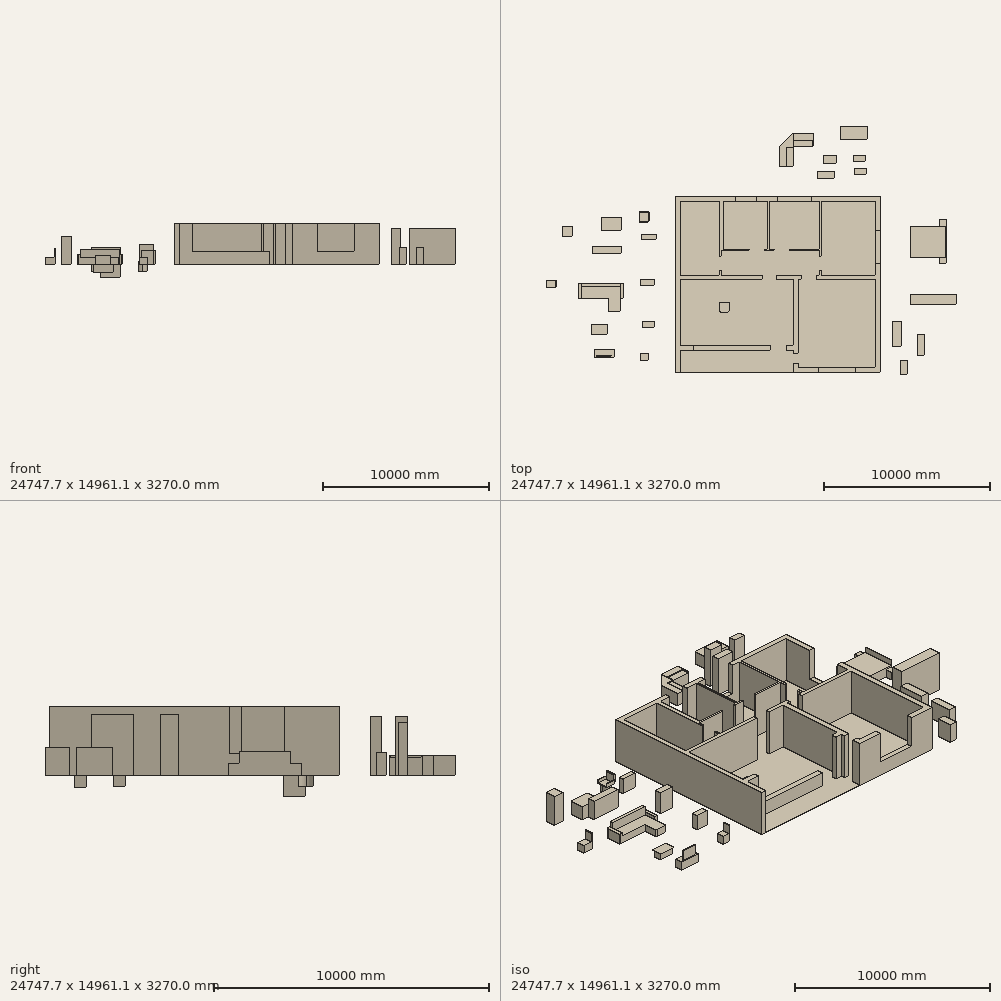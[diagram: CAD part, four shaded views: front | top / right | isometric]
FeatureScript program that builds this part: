
annotation { "Feature Type Name" : "Feature", "Feature Type Description" : "" }
export const myFeature = defineFeature(function(context is Context, id is Id, definition is map)
    precondition{}
    {
        {
            var Q0;
            Q0=qCreatedBy(makeId("Top.planeOp"),FACE);
            var sketch = newSketch(context, id + "F0", { "sketchPlane" : qUnion([Q0])});
            skLineSegment(sketch, "E0", {"start": v(0, 0) * mm, "end": v(12365, 0) * mm});
            skLineSegment(sketch, "E1", {"start": v(12365, 0) * mm, "end": v(12365, 10595) * mm});
            skLineSegment(sketch, "E2", {"start": v(12365, 10595) * mm, "end": v(0, 10595) * mm});
            skLineSegment(sketch, "E3", {"start": v(0, 10595) * mm, "end": v(0, 0) * mm});
            skLineSegment(sketch, "E4", {"start": v(12062.5, 10292.5) * mm, "end": v(12062.5, 5802.5) * mm});
            skLineSegment(sketch, "E5", {"start": v(12062.5, 302.5) * mm, "end": v(7427.5, 302.5) * mm});
            skLineSegment(sketch, "E6", {"start": v(7427.5, 302.5) * mm, "end": v(7427.5, 5562.5) * mm});
            skLineSegment(sketch, "E7", {"start": v(12062.5, 10292.5) * mm, "end": v(8802.5, 10292.5) * mm});
            skLineSegment(sketch, "E8", {"start": v(302.5, 10292.5) * mm, "end": v(302.5, 5802.5) * mm});
            skLineSegment(sketch, "E9", {"start": v(12062.5, 5562.5) * mm, "end": v(7427.5, 5562.5) * mm});
            skLineSegment(sketch, "E10", {"start": v(12062.5, 5802.5) * mm, "end": v(8802.5, 5802.5) * mm});
            skPoint(sketch, "E10.endSnap0", {"position": v(302.5, 5146.25) * mm});
            skLineSegment(sketch, "E11", {"start": v(7125, 5562.5) * mm, "end": v(7125, 1617.5) * mm});
            skLineSegment(sketch, "E12", {"start": v(8802.5, 10292.5) * mm, "end": v(8802.5, 5802.5) * mm});
            skLineSegment(sketch, "E13", {"start": v(8687.5, 10292.5) * mm, "end": v(8687.5, 7427.5) * mm});
            skLineSegment(sketch, "E14", {"start": v(8687.5, 7312.5) * mm, "end": v(2802.5, 7312.5) * mm});
            skLineSegment(sketch, "E15", {"start": v(2687.5, 10292.5) * mm, "end": v(2687.5, 7312.5) * mm});
            skLineSegment(sketch, "E16", {"start": v(2927.5, 10292.5) * mm, "end": v(2927.5, 7427.5) * mm});
            skLineSegment(sketch, "E17", {"start": v(2927.5, 7427.5) * mm, "end": v(5562.5, 7427.5) * mm});
            skLineSegment(sketch, "E18", {"start": v(2687.5, 7312.5) * mm, "end": v(2687.5, 5802.5) * mm});
            skLineSegment(sketch, "E19", {"start": v(2802.5, 7312.5) * mm, "end": v(2802.5, 5802.5) * mm});
            skLineSegment(sketch, "E20", {"start": v(5677.5, 10292.5) * mm, "end": v(5677.5, 7427.5) * mm});
            skLineSegment(sketch, "E21", {"start": v(5562.5, 10292.5) * mm, "end": v(5562.5, 7427.5) * mm});
            skLineSegment(sketch, "E22.trimOffspring", {"start": v(2687.5, 10292.5) * mm, "end": v(302.5, 10292.5) * mm});
            skLineSegment(sketch, "E23.trimOffspring", {"start": v(5562.5, 10292.5) * mm, "end": v(2927.5, 10292.5) * mm});
            skLineSegment(sketch, "E24.trimOffspring", {"start": v(5677.5, 7427.5) * mm, "end": v(8687.5, 7427.5) * mm});
            skLineSegment(sketch, "E25.trimOffspring", {"start": v(8687.5, 10292.5) * mm, "end": v(5677.5, 10292.5) * mm});
            skLineSegment(sketch, "E26.trimOffspring", {"start": v(8687.5, 7312.5) * mm, "end": v(8687.5, 5802.5) * mm});
            skLineSegment(sketch, "E27.trimOffspring", {"start": v(12062.5, 5562.5) * mm, "end": v(12062.5, 302.5) * mm});
            skLineSegment(sketch, "E28.trimOffspring", {"start": v(302.5, 5562.5) * mm, "end": v(302.5, 1617.5) * mm});
            skLineSegment(sketch, "E29.trimOffspring", {"start": v(2687.5, 5802.5) * mm, "end": v(302.5, 5802.5) * mm});
            skLineSegment(sketch, "E30", {"start": v(302.5, 1315) * mm, "end": v(7125, 1315) * mm});
            skLineSegment(sketch, "E31", {"start": v(302.5, 1617.5) * mm, "end": v(7125, 1617.5) * mm});
            skLineSegment(sketch, "E32.trimOffspring", {"start": v(302.5, 1315) * mm, "end": v(302.5, 0) * mm});
            skLineSegment(sketch, "E33.trimOffspring", {"start": v(7125, 1315) * mm, "end": v(7125, 0) * mm});
            skLineSegment(sketch, "E34.trimOffspring", {"start": v(7125, 5562.5) * mm, "end": v(302.5, 5562.5) * mm});
            skLineSegment(sketch, "E35", {"start": v(8687.5, 7000) * mm, "end": v(8802.5, 7000) * mm});
            skLineSegment(sketch, "E36", {"start": v(8687.5, 6115) * mm, "end": v(8802.5, 6115) * mm});
            skLineSegment(sketch, "E37.trimOffspring", {"start": v(8687.5, 5802.5) * mm, "end": v(2802.5, 5802.5) * mm});
            skLineSegment(sketch, "E38", {"start": v(7615, 5802.5) * mm, "end": v(7615, 5562.5) * mm});
            skLineSegment(sketch, "E39", {"start": v(8500, 5802.5) * mm, "end": v(8500, 5562.5) * mm});
            skLineSegment(sketch, "E40", {"start": v(5990, 7427.5) * mm, "end": v(5990, 7312.5) * mm});
            skLineSegment(sketch, "E41", {"start": v(6875, 7427.5) * mm, "end": v(6875, 7312.5) * mm});
            skLineSegment(sketch, "E42", {"start": v(5375, 7427.5) * mm, "end": v(5375, 7312.5) * mm});
            skLineSegment(sketch, "E43", {"start": v(4490, 7427.5) * mm, "end": v(4490, 7312.5) * mm});
            skLineSegment(sketch, "E44", {"start": v(6125, 5802.5) * mm, "end": v(6125, 5562.5) * mm});
            skLineSegment(sketch, "E45", {"start": v(5240, 5802.5) * mm, "end": v(5240, 5562.5) * mm});
            skLineSegment(sketch, "E46", {"start": v(8615, 302.5) * mm, "end": v(8615, 0) * mm});
            skLineSegment(sketch, "E47", {"start": v(10875, 302.5) * mm, "end": v(10875, 0) * mm});
            skLineSegment(sketch, "E48", {"start": v(1102.5, 1617.5) * mm, "end": v(1102.5, 1315) * mm});
            skLineSegment(sketch, "E49", {"start": v(6725, 1617.5) * mm, "end": v(6725, 1315) * mm});
            skLineSegment(sketch, "E50", {"start": v(7125, 1108.75) * mm, "end": v(7427.5, 1108.75) * mm});
            skLineSegment(sketch, "E51", {"start": v(7125, 508.75) * mm, "end": v(7427.5, 508.75) * mm});
            skLineSegment(sketch, "E52", {"start": v(12062.5, 8572.5) * mm, "end": v(12365, 8572.5) * mm});
            skLineSegment(sketch, "E53", {"start": v(12062.5, 6562.5) * mm, "end": v(12365, 6562.5) * mm});
            skArc(sketch, "E54", {"start": v(8802.5, 7000) * mm, "mid": v(9428.29, 6740.79) * mm, "end": v(9687.5, 6115) * mm});
            skArc(sketch, "E55", {"start": v(6875, 7427.5) * mm, "mid": v(6615.79, 8053.29) * mm, "end": v(5990, 8312.5) * mm});
            skArc(sketch, "E56", {"start": v(4490, 7427.5) * mm, "mid": v(4749.21, 8053.29) * mm, "end": v(5375, 8312.5) * mm});
            skArc(sketch, "E57", {"start": v(5240, 5562.5) * mm, "mid": v(5499.21, 4936.71) * mm, "end": v(6125, 4677.5) * mm});
            skArc(sketch, "E58", {"start": v(7427.5, 1108.75) * mm, "mid": v(7851.76, 933.01) * mm, "end": v(8027.5, 508.75) * mm});
            skLineSegment(sketch, "E59", {"start": v(5715, 1617.5) * mm, "end": v(5715, 1315) * mm});
            skArc(sketch, "E60", {"start": v(5715, 1617.5) * mm, "mid": v(6010.82, 2331.68) * mm, "end": v(6725, 2627.5) * mm});
            skLineSegment(sketch, "E61", {"start": v(2687.5, 7000) * mm, "end": v(2802.5, 7000) * mm});
            skLineSegment(sketch, "E62", {"start": v(2687.5, 6115) * mm, "end": v(2802.5, 6115) * mm});
            skArc(sketch, "E63", {"start": v(8500, 5562.5) * mm, "mid": v(8240.79, 4936.71) * mm, "end": v(7615, 4677.5) * mm});
            skLineSegment(sketch, "E64", {"start": v(6177.5, 10595) * mm, "end": v(6177.5, 10292.5) * mm});
            skLineSegment(sketch, "E65", {"start": v(8187.5, 10595) * mm, "end": v(8187.5, 10292.5) * mm});
            skLineSegment(sketch, "E66", {"start": v(3615, 10595) * mm, "end": v(3615, 10292.5) * mm});
            skLineSegment(sketch, "E67", {"start": v(4875, 10595) * mm, "end": v(4875, 10292.5) * mm});
            skSolve(sketch);
        }
        {
            var Q0;
            Q0=qCreatedBy(makeId("Top.planeOp"),FACE);
            var sketch = newSketch(context, id + "F1", { "sketchPlane" : qUnion([Q0])});
            skLineSegment(sketch, "E68.bottom", {"start": v(0, 0) * mm, "end": v(12364.74, 0) * mm});
            skLineSegment(sketch, "E68.top", {"start": v(0, 10595.95) * mm, "end": v(12364.74, 10595.95) * mm});
            skLineSegment(sketch, "E68.left", {"start": v(0, 0) * mm, "end": v(0, 10595.95) * mm});
            skLineSegment(sketch, "E68.right", {"start": v(12364.74, 0) * mm, "end": v(12364.74, 10595.95) * mm});
            skSolve(sketch);
        }
        {
            var Q0;
            {var subQ12=sQuery(id+"F0.wireOp",EDGE,"E10");Q0=makeQuery(id+"F0.imprint","IMPRINT",FACE,{"disambiguationData":[TD([[makeQuery(id+"F0.imprint","IMPRINT",EDGE,{"derivedFrom":subQ12}),1.0]])]});}
            var Q1;
            {var subQ8=sQuery(id+"F0.wireOp",EDGE,"E11");Q1=makeQuery(id+"F0.imprint","IMPRINT",FACE,{"disambiguationData":[TD([[makeQuery(id+"F0.imprint","IMPRINT",EDGE,{"derivedFrom":subQ8}),1.0]])]});}
            var Q2;
            {var subQ7=sQuery(id+"F0.wireOp",EDGE,"E46");Q2=makeQuery(id+"F0.imprint","IMPRINT",FACE,{"disambiguationData":[TD([[makeQuery(id+"F0.imprint","IMPRINT",EDGE,{"derivedFrom":subQ7}),-1.0]])]});}
            var Q3;
            {var subQ21=sQuery(id+"F0.wireOp",EDGE,"E3");Q3=makeQuery(id+"F0.imprint","IMPRINT",FACE,{"disambiguationData":[TD([[makeQuery(id+"F0.imprint","IMPRINT",EDGE,{"derivedFrom":subQ21}),1.0]])]});}
            var Q4;
            {var subQ3=sQuery(id+"F0.wireOp",EDGE,"E20");Q4=makeQuery(id+"F0.imprint","IMPRINT",FACE,{"disambiguationData":[TD([[makeQuery(id+"F0.imprint","IMPRINT",EDGE,{"derivedFrom":subQ3}),-1.0]])]});}
            var Q5;
            {var subQ4=sQuery(id+"F0.wireOp",EDGE,"E7");Q5=makeQuery(id+"F0.imprint","IMPRINT",FACE,{"disambiguationData":[TD([[makeQuery(id+"F0.imprint","IMPRINT",EDGE,{"derivedFrom":subQ4}),-1.0]])]});}
            extrude(context, id + "F2", {"entities" : qUnion([Q0, Q1, Q2, Q3, Q4, Q5]), "depth" : 2500 * mm});
        }
        {
            var Q0;
            {var subQ0=sQuery(id+"F0.wireOp",EDGE,"E52");Q0=makeQuery(id+"F0.imprint","IMPRINT",FACE,{"disambiguationData":[TD([[makeQuery(id+"F0.imprint","IMPRINT",EDGE,{"derivedFrom":subQ0}),-1.0]])]});}
            var Q1;
            {var subQ0=sQuery(id+"F0.wireOp",EDGE,"E46");Q1=makeQuery(id+"F0.imprint","IMPRINT",FACE,{"disambiguationData":[TD([[makeQuery(id+"F0.imprint","IMPRINT",EDGE,{"derivedFrom":subQ0}),1.0]])]});}
            var Q2;
            {var subQ0=sQuery(id+"F0.wireOp",EDGE,"E48");Q2=makeQuery(id+"F0.imprint","IMPRINT",FACE,{"disambiguationData":[TD([[makeQuery(id+"F0.imprint","IMPRINT",EDGE,{"derivedFrom":subQ0}),1.0]])]});}
            var Q3;
            {var subQ0=sQuery(id+"F0.wireOp",EDGE,"E66");Q3=makeQuery(id+"F0.imprint","IMPRINT",FACE,{"disambiguationData":[TD([[makeQuery(id+"F0.imprint","IMPRINT",EDGE,{"derivedFrom":subQ0}),1.0]])]});}
            var Q4;
            {var subQ0=sQuery(id+"F0.wireOp",EDGE,"E64");Q4=makeQuery(id+"F0.imprint","IMPRINT",FACE,{"disambiguationData":[TD([[makeQuery(id+"F0.imprint","IMPRINT",EDGE,{"derivedFrom":subQ0}),1.0]])]});}
            extrude(context, id + "F3", {"entities" : qUnion([Q0, Q1, Q2, Q3, Q4]), "operationType" : NewBodyOperationType.ADD, "depth" : 800 * mm});
        }
        {
            var Q0;
            Q0 = qSketchRegion(id + "F1", true);
            extrude(context, id + "F4", {"entities" : qUnion([Q0]), "operationType" : NewBodyOperationType.ADD, "depth" : 25 * mm});
        }
        {
            var Q0;
            {var subQ3=sQuery(id+"F0.wireOp",EDGE,"E7");var subQ55=sQuery(id+"F1.wireOp",EDGE,"E68.bottom");Q0=makeQuery(id+"F4.boolean.opBoolean","SPLIT",FACE,{"disambiguationData":[TD([makeQuery(id+"F2.opExtrude","SWEPT_FACE",FACE,{"disambiguationData":[OSD([subQ3])]})])],"derivedFrom":makeQuery(id+"F4.opExtrude","CAP_FACE",FACE,{"disambiguationData":[OSD([subQ55,sQuery(id+"F1.wireOp",EDGE,"E68.top"),sQuery(id+"F1.wireOp",EDGE,"E68.left"),sQuery(id+"F1.wireOp",EDGE,"E68.right")])],"isStart":false})});}
            var sketch = newSketch(context, id + "F5", { "sketchPlane" : qUnion([Q0])});
            skLineSegment(sketch, "E69.bottom", {"start": v(2725.04, 4227.94) * mm, "end": v(3195.04, 4227.94) * mm});
            skLineSegment(sketch, "E69.top", {"start": v(2725.04, 3627.94) * mm, "end": v(3195.04, 3627.94) * mm});
            skLineSegment(sketch, "E69.left", {"start": v(2675.04, 4177.94) * mm, "end": v(2675.04, 3677.94) * mm});
            skLineSegment(sketch, "E69.right", {"start": v(3245.04, 4177.94) * mm, "end": v(3245.04, 3677.94) * mm});
            skPoint(sketch, "E70.visualSharp", {"position": v(2675.04, 4227.94) * mm});
            skArc(sketch, "E70.filletArc", {"start": v(2725.04, 4227.94) * mm, "mid": v(2689.69, 4213.3) * mm, "end": v(2675.04, 4177.94) * mm});
            skPoint(sketch, "E71.visualSharp", {"position": v(3245.04, 4227.94) * mm});
            skArc(sketch, "E71.filletArc", {"start": v(3245.04, 4177.94) * mm, "mid": v(3230.4, 4213.3) * mm, "end": v(3195.04, 4227.94) * mm});
            skPoint(sketch, "E72.visualSharp", {"position": v(3245.04, 3627.94) * mm});
            skArc(sketch, "E72.filletArc", {"start": v(3195.04, 3627.94) * mm, "mid": v(3230.4, 3642.58) * mm, "end": v(3245.04, 3677.94) * mm});
            skPoint(sketch, "E73.visualSharp", {"position": v(2675.04, 3627.94) * mm});
            skArc(sketch, "E73.filletArc", {"start": v(2675.04, 3677.94) * mm, "mid": v(2689.69, 3642.58) * mm, "end": v(2725.04, 3627.94) * mm});
            skSolve(sketch);
        }
        {
            var Q0;
            Q0 = qSketchRegion(id + "F5", true);
            extrude(context, id + "F6", {"entities" : qUnion([Q0]), "depth" : 400 * mm});
        }
        {
            var Q0;
            {var subQ3=sQuery(id+"F0.wireOp",EDGE,"E7");var subQ55=sQuery(id+"F1.wireOp",EDGE,"E68.bottom");Q0=makeQuery(id+"F4.boolean.opBoolean","SPLIT",FACE,{"disambiguationData":[TD([makeQuery(id+"F2.opExtrude","SWEPT_FACE",FACE,{"disambiguationData":[OSD([subQ3])]})])],"derivedFrom":makeQuery(id+"F4.opExtrude","CAP_FACE",FACE,{"disambiguationData":[OSD([subQ55,sQuery(id+"F1.wireOp",EDGE,"E68.top"),sQuery(id+"F1.wireOp",EDGE,"E68.left"),sQuery(id+"F1.wireOp",EDGE,"E68.right")])],"isStart":false})});}
            var sketch = newSketch(context, id + "F7", { "sketchPlane" : qUnion([Q0])});
            skLineSegment(sketch, "E74", {"start": v(-5864.13, 4489.84) * mm, "end": v(-5864.13, 5289.84) * mm});
            skLineSegment(sketch, "E75", {"start": v(-5814.13, 5339.84) * mm, "end": v(-3164.13, 5339.84) * mm});
            skLineSegment(sketch, "E76", {"start": v(-3114.13, 5289.84) * mm, "end": v(-3114.13, 4489.84) * mm});
            skLineSegment(sketch, "E77", {"start": v(-3164.13, 4439.84) * mm, "end": v(-3314.13, 4439.84) * mm});
            skLineSegment(sketch, "E78", {"start": v(-3314.13, 4439.84) * mm, "end": v(-3314.13, 3689.84) * mm});
            skLineSegment(sketch, "E79", {"start": v(-3364.13, 3639.84) * mm, "end": v(-3964.13, 3639.84) * mm});
            skLineSegment(sketch, "E80", {"start": v(-4014.13, 3689.84) * mm, "end": v(-4014.13, 4439.84) * mm});
            skLineSegment(sketch, "E81", {"start": v(-4014.13, 4439.84) * mm, "end": v(-5814.13, 4439.84) * mm});
            skLineSegment(sketch, "E82", {"start": v(-4014.13, 4439.84) * mm, "end": v(-3314.13, 4439.84) * mm, "construction": true});
            skLineSegment(sketch, "E83", {"start": v(-5664.13, 5339.84) * mm, "end": v(-5664.13, 4439.84) * mm});
            skLineSegment(sketch, "E84", {"start": v(-3314.13, 4439.84) * mm, "end": v(-3314.13, 5339.84) * mm});
            skLineSegment(sketch, "E85", {"start": v(-5664.13, 5139.84) * mm, "end": v(-3314.13, 5139.84) * mm});
            skPoint(sketch, "E86.visualSharp", {"position": v(-5864.13, 4439.84) * mm});
            skArc(sketch, "E86.filletArc", {"start": v(-5864.13, 4489.84) * mm, "mid": v(-5849.48, 4454.48) * mm, "end": v(-5814.13, 4439.84) * mm});
            skPoint(sketch, "E87.visualSharp", {"position": v(-4014.13, 3639.84) * mm});
            skArc(sketch, "E87.filletArc", {"start": v(-4014.13, 3689.84) * mm, "mid": v(-3999.48, 3654.48) * mm, "end": v(-3964.13, 3639.84) * mm});
            skPoint(sketch, "E88.visualSharp", {"position": v(-3314.13, 3639.84) * mm});
            skArc(sketch, "E88.filletArc", {"start": v(-3364.13, 3639.84) * mm, "mid": v(-3328.77, 3654.48) * mm, "end": v(-3314.13, 3689.84) * mm});
            skPoint(sketch, "E89.visualSharp", {"position": v(-3114.13, 4439.84) * mm});
            skArc(sketch, "E89.filletArc", {"start": v(-3164.13, 4439.84) * mm, "mid": v(-3128.77, 4454.48) * mm, "end": v(-3114.13, 4489.84) * mm});
            skPoint(sketch, "E90.visualSharp", {"position": v(-3114.13, 5339.84) * mm});
            skArc(sketch, "E90.filletArc", {"start": v(-3114.13, 5289.84) * mm, "mid": v(-3128.77, 5325.2) * mm, "end": v(-3164.13, 5339.84) * mm});
            skPoint(sketch, "E91.visualSharp", {"position": v(-5864.13, 5339.84) * mm});
            skArc(sketch, "E91.filletArc", {"start": v(-5814.13, 5339.84) * mm, "mid": v(-5849.48, 5325.2) * mm, "end": v(-5864.13, 5289.84) * mm});
            skSolve(sketch);
        }
        {
            var Q0;
            Q0 = qSketchRegion(id + "F7", true);
            extrude(context, id + "F8", {"entities" : qUnion([Q0]), "depth" : 400 * mm});
        }
        {
            var Q0;
            Q0=makeQuery(id+"F7.imprint","IMPRINT",FACE,{"disambiguationData":[TD([[makeQuery(id+"F7.imprint","IMPRINT",EDGE,{"derivedFrom":sQuery(id+"F7.wireOp",EDGE,"E74")}),-1.0]])]});
            var Q1;
            Q1=makeQuery(id+"F7.imprint","IMPRINT",FACE,{"disambiguationData":[TD([[makeQuery(id+"F7.imprint","IMPRINT",EDGE,{"derivedFrom":sQuery(id+"F7.wireOp",EDGE,"E76")}),-1.0]])]});
            extrude(context, id + "F9", {"entities" : qUnion([Q0, Q1]), "operationType" : NewBodyOperationType.ADD, "depth" : 580 * mm});
        }
        {
            var Q0;
            {var subQ5=sQuery(id+"F7.wireOp",EDGE,"E85");Q0=makeQuery(id+"F7.imprint","IMPRINT",FACE,{"disambiguationData":[TD([[makeQuery(id+"F7.imprint","IMPRINT",EDGE,{"derivedFrom":subQ5}),1.0]])]});}
            extrude(context, id + "F10", {"entities" : qUnion([Q0]), "operationType" : NewBodyOperationType.ADD, "depth" : 900 * mm});
        }
        {
            var Q0;
            Q0=qCreatedBy(makeId("Top.planeOp"),FACE);
            var sketch = newSketch(context, id + "F11", { "sketchPlane" : qUnion([Q0])});
            skLineSegment(sketch, "E92.bottom", {"start": v(-5079.16, 2851.6) * mm, "end": v(-4079.16, 2851.6) * mm});
            skLineSegment(sketch, "E92.top", {"start": v(-5079.16, 2251.6) * mm, "end": v(-4079.16, 2251.6) * mm});
            skLineSegment(sketch, "E92.left", {"start": v(-5079.16, 2851.6) * mm, "end": v(-5079.16, 2251.6) * mm});
            skLineSegment(sketch, "E92.right", {"start": v(-4079.16, 2851.6) * mm, "end": v(-4079.16, 2251.6) * mm});
            skLineSegment(sketch, "E93.0", {"start": v(-5004.16, 2776.6) * mm, "end": v(-4154.16, 2776.6) * mm});
            skLineSegment(sketch, "E93.1", {"start": v(-5004.16, 2776.6) * mm, "end": v(-5004.16, 2326.6) * mm});
            skLineSegment(sketch, "E93.2", {"start": v(-5004.16, 2326.6) * mm, "end": v(-4154.16, 2326.6) * mm});
            skLineSegment(sketch, "E93.3", {"start": v(-4154.16, 2776.6) * mm, "end": v(-4154.16, 2326.6) * mm});
            skSolve(sketch);
        }
        {
            var Q0;
            Q0=makeQuery(id+"F11.imprint","IMPRINT",FACE,{"disambiguationData":[TD([[makeQuery(id+"F11.imprint","IMPRINT",EDGE,{"derivedFrom":sQuery(id+"F11.wireOp",EDGE,"E93.0")}),-1.0]])]});
            extrude(context, id + "F12", {"entities" : qUnion([Q0]), "oppositeDirection" : true, "depth" : 395 * mm});
        }
        {
            var Q0;
            Q0 = qSketchRegion(id + "F11", true);
            var Q1;
            Q1=makeQuery(id+"F11.imprint","IMPRINT",FACE,{"disambiguationData":[TD([[makeQuery(id+"F11.imprint","IMPRINT",EDGE,{"derivedFrom":sQuery(id+"F11.wireOp",EDGE,"E93.0")}),-1.0]])]});
            extrude(context, id + "F13", {"entities" : qUnion([Q0, Q1]), "operationType" : NewBodyOperationType.ADD, "depth" : 5 * mm});
        }
        {
            var Q0;
            Q0=qCreatedBy(makeId("Top.planeOp"),FACE);
            var sketch = newSketch(context, id + "F14", { "sketchPlane" : qUnion([Q0])});
            skLineSegment(sketch, "E94.bottom", {"start": v(-4892.25, 1350.75) * mm, "end": v(-3692.25, 1350.75) * mm});
            skLineSegment(sketch, "E94.top", {"start": v(-4892.25, 900.75) * mm, "end": v(-3692.25, 900.75) * mm});
            skLineSegment(sketch, "E94.left", {"start": v(-4892.25, 1350.75) * mm, "end": v(-4892.25, 900.75) * mm});
            skLineSegment(sketch, "E94.right", {"start": v(-3692.25, 1350.75) * mm, "end": v(-3692.25, 900.75) * mm});
            skLineSegment(sketch, "E95.bottom", {"start": v(-4742.25, 1029.75) * mm, "end": v(-3842.25, 1029.75) * mm});
            skLineSegment(sketch, "E95.top", {"start": v(-4742.25, 969.75) * mm, "end": v(-3842.25, 969.75) * mm});
            skLineSegment(sketch, "E95.left", {"start": v(-4742.25, 1029.75) * mm, "end": v(-4742.25, 969.75) * mm});
            skLineSegment(sketch, "E95.right", {"start": v(-3842.25, 1029.75) * mm, "end": v(-3842.25, 969.75) * mm});
            skSolve(sketch);
        }
        {
            var Q0;
            Q0 = qSketchRegion(id + "F14", true);
            var Q1;
            Q1=makeQuery(id+"F14.imprint","IMPRINT",FACE,{"disambiguationData":[TD([[makeQuery(id+"F14.imprint","IMPRINT",EDGE,{"derivedFrom":sQuery(id+"F14.wireOp",EDGE,"E95.bottom")}),-1.0]])]});
            extrude(context, id + "F15", {"entities" : qUnion([Q0, Q1]), "oppositeDirection" : true, "depth" : 460 * mm});
        }
        {
            var Q0;
            Q0=makeQuery(id+"F14.imprint","IMPRINT",FACE,{"disambiguationData":[TD([[makeQuery(id+"F14.imprint","IMPRINT",EDGE,{"derivedFrom":sQuery(id+"F14.wireOp",EDGE,"E95.bottom")}),-1.0]])]});
            extrude(context, id + "F16", {"entities" : qUnion([Q0]), "operationType" : NewBodyOperationType.ADD, "depth" : 580 * mm});
        }
        {
            var Q0;
            Q0=qCreatedBy(makeId("Top.planeOp"),FACE);
            var sketch = newSketch(context, id + "F17", { "sketchPlane" : qUnion([Q0])});
            skLineSegment(sketch, "E96.bottom", {"start": v(-4974.58, 7585.4) * mm, "end": v(-3244.58, 7585.4) * mm});
            skLineSegment(sketch, "E96.top", {"start": v(-4974.58, 7185.4) * mm, "end": v(-3244.58, 7185.4) * mm});
            skLineSegment(sketch, "E96.left", {"start": v(-4974.58, 7585.4) * mm, "end": v(-4974.58, 7185.4) * mm});
            skLineSegment(sketch, "E96.right", {"start": v(-3244.58, 7585.4) * mm, "end": v(-3244.58, 7185.4) * mm});
            skSolve(sketch);
        }
        {
            var Q0;
            Q0 = qSketchRegion(id + "F17", true);
            extrude(context, id + "F18", {"entities" : qUnion([Q0]), "depth" : 1070 * mm});
        }
        {
            var Q0;
            Q0=qCreatedBy(makeId("Top.planeOp"),FACE);
            var sketch = newSketch(context, id + "F19", { "sketchPlane" : qUnion([Q0])});
            skLineSegment(sketch, "E97.bottom", {"start": v(-4870.5, 9345.17) * mm, "end": v(-2870.5, 9345.17) * mm});
            skLineSegment(sketch, "E97.top", {"start": v(-4870.5, 8545.17) * mm, "end": v(-2870.5, 8545.17) * mm});
            skLineSegment(sketch, "E97.left", {"start": v(-4870.5, 9345.17) * mm, "end": v(-4870.5, 8545.17) * mm});
            skLineSegment(sketch, "E97.right", {"start": v(-2870.5, 9345.17) * mm, "end": v(-2870.5, 8545.17) * mm});
            skLineSegment(sketch, "E98", {"start": v(-4470.5, 9345.17) * mm, "end": v(-4470.5, 8545.17) * mm});
            skLineSegment(sketch, "E99", {"start": v(-3270.5, 9345.17) * mm, "end": v(-3270.5, 8545.17) * mm});
            skSolve(sketch);
        }
        {
            var Q0;
            {var subQ0=sQuery(id+"F19.wireOp",EDGE,"E98");Q0=makeQuery(id+"F19.imprint","IMPRINT",FACE,{"disambiguationData":[TD([[makeQuery(id+"F19.imprint","IMPRINT",EDGE,{"derivedFrom":subQ0}),1.0]])]});}
            extrude(context, id + "F20", {"entities" : qUnion([Q0]), "oppositeDirection" : true, "depth" : 30 * mm});
        }
        {
            var Q0;
            {var subQ0=sQuery(id+"F19.wireOp",EDGE,"E98");Q0=makeQuery(id+"F19.imprint","IMPRINT",FACE,{"disambiguationData":[TD([[makeQuery(id+"F19.imprint","IMPRINT",EDGE,{"derivedFrom":subQ0}),1.0]])]});}
            extrude(context, id + "F21", {"entities" : qUnion([Q0]), "operationType" : NewBodyOperationType.ADD, "oppositeDirection" : true, "depth" : 770 * mm});
        }
        {
            var Q0;
            Q0=qCreatedBy(makeId("Top.planeOp"),FACE);
            var sketch = newSketch(context, id + "F22", { "sketchPlane" : qUnion([Q0])});
            skLineSegment(sketch, "E100.bottom", {"start": v(-7779.5, 5559.42) * mm, "end": v(-7179.5, 5559.42) * mm});
            skLineSegment(sketch, "E100.top", {"start": v(-7779.5, 5109.42) * mm, "end": v(-7179.5, 5109.42) * mm});
            skLineSegment(sketch, "E100.left", {"start": v(-7779.5, 5559.42) * mm, "end": v(-7779.5, 5109.42) * mm});
            skLineSegment(sketch, "E100.right", {"start": v(-7179.5, 5559.42) * mm, "end": v(-7179.5, 5109.42) * mm});
            skLineSegment(sketch, "E101", {"start": v(-7239.5, 5559.42) * mm, "end": v(-7239.5, 5109.42) * mm});
            skSolve(sketch);
        }
        {
            var Q0;
            Q0 = qSketchRegion(id + "F22", true);
            extrude(context, id + "F23", {"entities" : qUnion([Q0]), "depth" : 450 * mm});
        }
        {
            var Q0;
            {var subQ0=sQuery(id+"F22.wireOp",EDGE,"E100.right");Q0=makeQuery(id+"F22.imprint","IMPRINT",FACE,{"disambiguationData":[TD([[makeQuery(id+"F22.imprint","IMPRINT",EDGE,{"derivedFrom":subQ0}),-1.0]])]});}
            extrude(context, id + "F24", {"entities" : qUnion([Q0]), "operationType" : NewBodyOperationType.ADD, "depth" : 960 * mm});
        }
        {
            var Q0;
            Q0=qCreatedBy(makeId("Top.planeOp"),FACE);
            var sketch = newSketch(context, id + "F25", { "sketchPlane" : qUnion([Q0])});
            skLineSegment(sketch, "E102.bottom", {"start": v(14218.24, 4713.84) * mm, "end": v(16968.24, 4713.84) * mm});
            skLineSegment(sketch, "E102.top", {"start": v(14218.24, 4053.84) * mm, "end": v(16968.24, 4053.84) * mm});
            skLineSegment(sketch, "E102.left", {"start": v(14218.24, 4713.84) * mm, "end": v(14218.24, 4053.84) * mm});
            skLineSegment(sketch, "E102.right", {"start": v(16968.24, 4713.84) * mm, "end": v(16968.24, 4053.84) * mm});
            skSolve(sketch);
        }
        {
            var Q0;
            Q0 = qSketchRegion(id + "F25", true);
            extrude(context, id + "F26", {"entities" : qUnion([Q0]), "depth" : 2200 * mm});
        }
        {
            var Q0;
            Q0=qCreatedBy(makeId("Top.planeOp"),FACE);
            var sketch = newSketch(context, id + "F27", { "sketchPlane" : qUnion([Q0])});
            skLineSegment(sketch, "E103.bottom", {"start": v(13130.87, 3056.08) * mm, "end": v(13630.87, 3056.08) * mm});
            skLineSegment(sketch, "E103.top", {"start": v(13130.87, 1556.08) * mm, "end": v(13630.87, 1556.08) * mm});
            skLineSegment(sketch, "E103.left", {"start": v(13130.87, 3056.08) * mm, "end": v(13130.87, 1556.08) * mm});
            skLineSegment(sketch, "E103.right", {"start": v(13630.87, 3056.08) * mm, "end": v(13630.87, 1556.08) * mm});
            skSolve(sketch);
        }
        {
            var Q0;
            Q0 = qSketchRegion(id + "F27", true);
            extrude(context, id + "F28", {"entities" : qUnion([Q0]), "depth" : 2200 * mm});
        }
        {
            var Q0;
            Q0=qCreatedBy(makeId("Top.planeOp"),FACE);
            var sketch = newSketch(context, id + "F29", { "sketchPlane" : qUnion([Q0])});
            skLineSegment(sketch, "E104.bottom", {"start": v(14216.94, 8797.36) * mm, "end": v(16346.94, 8797.36) * mm});
            skLineSegment(sketch, "E104.top", {"start": v(14216.94, 6927.36) * mm, "end": v(16346.94, 6927.36) * mm});
            skLineSegment(sketch, "E104.left", {"start": v(14216.94, 8797.36) * mm, "end": v(14216.94, 6927.36) * mm});
            skLineSegment(sketch, "E104.right", {"start": v(16346.94, 8797.36) * mm, "end": v(16346.94, 6927.36) * mm});
            skLineSegment(sketch, "E105", {"start": v(16346.94, 8797.36) * mm, "end": v(16346.94, 9197.36) * mm});
            skLineSegment(sketch, "E106", {"start": v(16346.94, 9197.36) * mm, "end": v(15946.94, 9197.36) * mm});
            skLineSegment(sketch, "E107", {"start": v(15946.94, 9197.36) * mm, "end": v(15946.94, 8797.36) * mm});
            skLineSegment(sketch, "E108", {"start": v(16346.94, 6927.36) * mm, "end": v(16346.94, 6527.36) * mm});
            skLineSegment(sketch, "E109", {"start": v(16346.94, 6527.36) * mm, "end": v(15946.94, 6527.36) * mm});
            skLineSegment(sketch, "E110", {"start": v(15946.94, 6527.36) * mm, "end": v(15946.94, 6927.36) * mm});
            skLineSegment(sketch, "E111", {"start": v(15946.94, 8797.36) * mm, "end": v(15946.94, 6927.36) * mm, "construction": true});
            skLineSegment(sketch, "E112", {"start": v(16316.94, 8797.36) * mm, "end": v(16316.94, 6927.36) * mm});
            skSolve(sketch);
        }
        {
            var Q0;
            {var subQ3=sQuery(id+"F29.wireOp",EDGE,"E104.left");Q0=makeQuery(id+"F29.imprint","IMPRINT",FACE,{"disambiguationData":[TD([[makeQuery(id+"F29.imprint","IMPRINT",EDGE,{"derivedFrom":subQ3}),1.0]])]});}
            var Q1;
            {var subQ0=sQuery(id+"F29.wireOp",EDGE,"E104.right");Q1=makeQuery(id+"F29.imprint","IMPRINT",FACE,{"disambiguationData":[TD([[makeQuery(id+"F29.imprint","IMPRINT",EDGE,{"derivedFrom":subQ0}),-1.0]])]});}
            extrude(context, id + "F30", {"entities" : qUnion([Q0, Q1]), "depth" : 550 * mm});
        }
        {
            var Q0;
            Q0 = qSketchRegion(id + "F29", true);
            extrude(context, id + "F31", {"entities" : qUnion([Q0]), "operationType" : NewBodyOperationType.ADD, "depth" : 440 * mm});
        }
        {
            var Q0;
            {var subQ0=sQuery(id+"F29.wireOp",EDGE,"E104.right");Q0=makeQuery(id+"F29.imprint","IMPRINT",FACE,{"disambiguationData":[TD([[makeQuery(id+"F29.imprint","IMPRINT",EDGE,{"derivedFrom":subQ0}),-1.0]])]});}
            extrude(context, id + "F32", {"entities" : qUnion([Q0]), "operationType" : NewBodyOperationType.ADD, "depth" : 870 * mm});
        }
        {
            var Q0;
            Q0=qCreatedBy(makeId("Top.planeOp"),FACE);
            var sketch = newSketch(context, id + "F33", { "sketchPlane" : qUnion([Q0])});
            skLineSegment(sketch, "E113.bottom", {"start": v(14619.27, 2288.8) * mm, "end": v(15049.27, 2288.8) * mm});
            skLineSegment(sketch, "E113.top", {"start": v(14619.27, 988.8) * mm, "end": v(15049.27, 988.8) * mm});
            skLineSegment(sketch, "E113.left", {"start": v(14619.27, 2288.8) * mm, "end": v(14619.27, 988.8) * mm});
            skLineSegment(sketch, "E113.right", {"start": v(15049.27, 2288.8) * mm, "end": v(15049.27, 988.8) * mm});
            skSolve(sketch);
        }
        {
            var Q0;
            Q0 = qSketchRegion(id + "F33", true);
            extrude(context, id + "F34", {"entities" : qUnion([Q0]), "depth" : 1025 * mm});
        }
        {
            var Q0;
            Q0=qCreatedBy(makeId("Top.planeOp"),FACE);
            var sketch = newSketch(context, id + "F35", { "sketchPlane" : qUnion([Q0])});
            skLineSegment(sketch, "E114.bottom", {"start": v(13562.25, 729.72) * mm, "end": v(13992.25, 729.72) * mm});
            skLineSegment(sketch, "E114.top", {"start": v(13562.25, -140.28) * mm, "end": v(13992.25, -140.28) * mm});
            skLineSegment(sketch, "E114.left", {"start": v(13562.25, 729.72) * mm, "end": v(13562.25, -140.28) * mm});
            skLineSegment(sketch, "E114.right", {"start": v(13992.25, 729.72) * mm, "end": v(13992.25, -140.28) * mm});
            skSolve(sketch);
        }
        {
            var Q0;
            Q0 = qSketchRegion(id + "F35", true);
            extrude(context, id + "F36", {"entities" : qUnion([Q0]), "depth" : 1025 * mm});
        }
        {
            var Q0;
            Q0=qCreatedBy(makeId("Top.planeOp"),FACE);
            var sketch = newSketch(context, id + "F37", { "sketchPlane" : qUnion([Q0])});
            skLineSegment(sketch, "E115.bottom", {"start": v(-6837.4, 8786.99) * mm, "end": v(-6237.4, 8786.99) * mm});
            skLineSegment(sketch, "E115.top", {"start": v(-6837.4, 8186.99) * mm, "end": v(-6237.4, 8186.99) * mm});
            skLineSegment(sketch, "E115.left", {"start": v(-6837.4, 8786.99) * mm, "end": v(-6837.4, 8186.99) * mm});
            skLineSegment(sketch, "E115.right", {"start": v(-6237.4, 8786.99) * mm, "end": v(-6237.4, 8186.99) * mm});
            skSolve(sketch);
        }
        {
            var Q0;
            Q0 = qSketchRegion(id + "F37", true);
            extrude(context, id + "F38", {"entities" : qUnion([Q0]), "depth" : 1700 * mm});
        }
        {
            var Q0;
            Q0=qCreatedBy(makeId("Top.planeOp"),FACE);
            var sketch = newSketch(context, id + "F39", { "sketchPlane" : qUnion([Q0])});
            skLineSegment(sketch, "E116.bottom", {"start": v(9978.66, 14820.8) * mm, "end": v(11578.66, 14820.8) * mm});
            skLineSegment(sketch, "E116.top", {"start": v(9978.66, 14020.8) * mm, "end": v(11578.66, 14020.8) * mm});
            skLineSegment(sketch, "E116.left", {"start": v(9978.66, 14820.8) * mm, "end": v(9978.66, 14020.8) * mm});
            skLineSegment(sketch, "E116.right", {"start": v(11578.66, 14820.8) * mm, "end": v(11578.66, 14020.8) * mm});
            skSolve(sketch);
        }
        {
            var Q0;
            Q0 = qSketchRegion(id + "F39", true);
            extrude(context, id + "F40", {"entities" : qUnion([Q0]), "depth" : 720 * mm});
        }
        {
            var Q0;
            Q0=qCreatedBy(makeId("Top.planeOp"),FACE);
            var sketch = newSketch(context, id + "F41", { "sketchPlane" : qUnion([Q0])});
            skLineSegment(sketch, "E117.bottom", {"start": v(7108.27, 14403.4) * mm, "end": v(8308.27, 14403.4) * mm});
            skLineSegment(sketch, "E117.top", {"start": v(7108.27, 13603.4) * mm, "end": v(8308.27, 13603.4) * mm});
            skLineSegment(sketch, "E117.left", {"start": v(7108.27, 14403.4) * mm, "end": v(7108.27, 13603.4) * mm});
            skLineSegment(sketch, "E117.right", {"start": v(8308.27, 14403.4) * mm, "end": v(8308.27, 13603.4) * mm});
            skLineSegment(sketch, "E118.bottom", {"start": v(7108.27, 13603.4) * mm, "end": v(6308.27, 13603.4) * mm});
            skLineSegment(sketch, "E118.top", {"start": v(7108.27, 12403.4) * mm, "end": v(6308.27, 12403.4) * mm});
            skLineSegment(sketch, "E118.left", {"start": v(7108.27, 13603.4) * mm, "end": v(7108.27, 12403.4) * mm});
            skLineSegment(sketch, "E118.right", {"start": v(6308.27, 13603.4) * mm, "end": v(6308.27, 12403.4) * mm});
            skLineSegment(sketch, "E119", {"start": v(7108.27, 14403.4) * mm, "end": v(6308.27, 13603.4) * mm});
            skLineSegment(sketch, "E120", {"start": v(7138.27, 13603.4) * mm, "end": v(7138.27, 14003.4) * mm});
            skLineSegment(sketch, "E121", {"start": v(7138.27, 14003.4) * mm, "end": v(8278.27, 14003.4) * mm});
            skLineSegment(sketch, "E122", {"start": v(8278.27, 14003.4) * mm, "end": v(8278.27, 13603.4) * mm});
            skLineSegment(sketch, "E123", {"start": v(7108.27, 13573.4) * mm, "end": v(6708.27, 13573.4) * mm});
            skLineSegment(sketch, "E124", {"start": v(6708.27, 13573.4) * mm, "end": v(6708.27, 12433.4) * mm});
            skLineSegment(sketch, "E125", {"start": v(6708.27, 12433.4) * mm, "end": v(7108.27, 12433.4) * mm});
            skSolve(sketch);
        }
        {
            var Q0;
            Q0=makeQuery(id+"F41.imprint","IMPRINT",FACE,{"disambiguationData":[TD([[makeQuery(id+"F41.imprint","IMPRINT",EDGE,{"derivedFrom":sQuery(id+"F41.wireOp",EDGE,"E117.left")}),-1.0]])]});
            var Q1;
            {var subQ3=sQuery(id+"F41.wireOp",EDGE,"E118.bottom");Q1=makeQuery(id+"F41.imprint","IMPRINT",FACE,{"disambiguationData":[TD([[makeQuery(id+"F41.imprint","IMPRINT",EDGE,{"derivedFrom":subQ3}),1.0]])]});}
            extrude(context, id + "F42", {"entities" : qUnion([Q0, Q1]), "depth" : 720 * mm});
        }
        {
            var Q0;
            {var subQ0=sQuery(id+"F41.wireOp",EDGE,"E123");Q0=makeQuery(id+"F41.imprint","IMPRINT",FACE,{"disambiguationData":[TD([[makeQuery(id+"F41.imprint","IMPRINT",EDGE,{"derivedFrom":subQ0}),1.0]])]});}
            extrude(context, id + "F43", {"entities" : qUnion([Q0]), "operationType" : NewBodyOperationType.ADD, "depth" : 650 * mm});
        }
        {
            var Q0;
            Q0=qCreatedBy(makeId("Top.planeOp"),FACE);
            var sketch = newSketch(context, id + "F44", { "sketchPlane" : qUnion([Q0])});
            skLineSegment(sketch, "E126.bottom", {"start": v(8917.94, 13064.97) * mm, "end": v(9717.94, 13064.97) * mm});
            skLineSegment(sketch, "E126.top", {"start": v(8917.94, 12614.97) * mm, "end": v(9717.94, 12614.97) * mm});
            skLineSegment(sketch, "E126.left", {"start": v(8917.94, 13064.97) * mm, "end": v(8917.94, 12614.97) * mm});
            skLineSegment(sketch, "E126.right", {"start": v(9717.94, 13064.97) * mm, "end": v(9717.94, 12614.97) * mm});
            skSolve(sketch);
        }
        {
            var Q0;
            Q0 = qSketchRegion(id + "F44", true);
            extrude(context, id + "F45", {"entities" : qUnion([Q0]), "depth" : 2140 * mm});
        }
        {
            var Q0;
            Q0=qCreatedBy(makeId("Top.planeOp"),FACE);
            var sketch = newSketch(context, id + "F46", { "sketchPlane" : qUnion([Q0])});
            skLineSegment(sketch, "E127.bottom", {"start": v(10759.27, 13086.65) * mm, "end": v(11479.27, 13086.65) * mm});
            skLineSegment(sketch, "E127.top", {"start": v(10759.27, 12736.65) * mm, "end": v(11479.27, 12736.65) * mm});
            skLineSegment(sketch, "E127.left", {"start": v(10759.27, 13086.65) * mm, "end": v(10759.27, 12736.65) * mm});
            skLineSegment(sketch, "E127.right", {"start": v(11479.27, 13086.65) * mm, "end": v(11479.27, 12736.65) * mm});
            skSolve(sketch);
        }
        {
            var Q0;
            Q0 = qSketchRegion(id + "F46", true);
            extrude(context, id + "F47", {"entities" : qUnion([Q0]), "depth" : 1940 * mm});
        }
        {
            var Q0;
            Q0=qCreatedBy(makeId("Top.planeOp"),FACE);
            var sketch = newSketch(context, id + "F48", { "sketchPlane" : qUnion([Q0])});
            skLineSegment(sketch, "E128.bottom", {"start": v(8555.7, 12112.2) * mm, "end": v(9595.7, 12112.2) * mm});
            skLineSegment(sketch, "E128.top", {"start": v(8555.7, 11712.2) * mm, "end": v(9595.7, 11712.2) * mm});
            skLineSegment(sketch, "E128.left", {"start": v(8555.7, 12112.2) * mm, "end": v(8555.7, 11712.2) * mm});
            skLineSegment(sketch, "E128.right", {"start": v(9595.7, 12112.2) * mm, "end": v(9595.7, 11712.2) * mm});
            skSolve(sketch);
        }
        {
            var Q0;
            Q0 = qSketchRegion(id + "F48", true);
            extrude(context, id + "F49", {"entities" : qUnion([Q0]), "depth" : 2150 * mm});
        }
        {
            var Q0;
            Q0=qCreatedBy(makeId("Top.planeOp"),FACE);
            var sketch = newSketch(context, id + "F50", { "sketchPlane" : qUnion([Q0])});
            skLineSegment(sketch, "E129.bottom", {"start": v(10818.74, 12293.86) * mm, "end": v(11538.74, 12293.86) * mm});
            skLineSegment(sketch, "E129.top", {"start": v(10818.74, 11943.86) * mm, "end": v(11538.74, 11943.86) * mm});
            skLineSegment(sketch, "E129.left", {"start": v(10818.74, 12293.86) * mm, "end": v(10818.74, 11943.86) * mm});
            skLineSegment(sketch, "E129.right", {"start": v(11538.74, 12293.86) * mm, "end": v(11538.74, 11943.86) * mm});
            skSolve(sketch);
        }
        {
            var Q0;
            Q0 = qSketchRegion(id + "F50", true);
            extrude(context, id + "F51", {"entities" : qUnion([Q0]), "depth" : 840 * mm});
        }
        {
            var Q0;
            Q0=qCreatedBy(makeId("Top.planeOp"),FACE);
            var sketch = newSketch(context, id + "F52", { "sketchPlane" : qUnion([Q0])});
            skLineSegment(sketch, "E130.right", {"start": v(-1616.75, 1152.82) * mm, "end": v(-1616.75, 702.82) * mm});
            skLineSegment(sketch, "E130.left", {"start": v(-2076.75, 1152.82) * mm, "end": v(-2076.75, 702.82) * mm});
            skLineSegment(sketch, "E130.top", {"start": v(-2076.75, 702.82) * mm, "end": v(-1616.75, 702.82) * mm});
            skLineSegment(sketch, "E131", {"start": v(-1646.75, 1152.82) * mm, "end": v(-1646.75, 702.82) * mm});
            skLineSegment(sketch, "E130.bottom", {"start": v(-2076.75, 1152.82) * mm, "end": v(-1616.75, 1152.82) * mm});
            skSolve(sketch);
        }
        {
            var Q0;
            Q0 = qSketchRegion(id + "F52", true);
            extrude(context, id + "F53", {"entities" : qUnion([Q0]), "depth" : 450 * mm});
        }
        {
            var Q0;
            {var subQ0=sQuery(id+"F52.wireOp",EDGE,"E130.right");Q0=makeQuery(id+"F52.imprint","IMPRINT",FACE,{"disambiguationData":[TD([[makeQuery(id+"F52.imprint","IMPRINT",EDGE,{"derivedFrom":subQ0}),-1.0]])]});}
            extrude(context, id + "F54", {"entities" : qUnion([Q0]), "operationType" : NewBodyOperationType.ADD, "depth" : 950 * mm});
        }
        {
            var Q0;
            Q0=qCreatedBy(makeId("Top.planeOp"),FACE);
            var sketch = newSketch(context, id + "F55", { "sketchPlane" : qUnion([Q0])});
            skLineSegment(sketch, "E132.bottom", {"start": v(-1997.66, 3047) * mm, "end": v(-1277.66, 3047) * mm});
            skLineSegment(sketch, "E132.top", {"start": v(-1997.66, 2697) * mm, "end": v(-1277.66, 2697) * mm});
            skLineSegment(sketch, "E132.left", {"start": v(-1997.66, 3047) * mm, "end": v(-1997.66, 2697) * mm});
            skLineSegment(sketch, "E132.right", {"start": v(-1277.66, 3047) * mm, "end": v(-1277.66, 2697) * mm});
            skSolve(sketch);
        }
        {
            var Q0;
            Q0 = qSketchRegion(id + "F55", true);
            extrude(context, id + "F56", {"entities" : qUnion([Q0]), "depth" : 840 * mm});
        }
        {
            var Q0;
            Q0=qCreatedBy(makeId("Top.planeOp"),FACE);
            var sketch = newSketch(context, id + "F57", { "sketchPlane" : qUnion([Q0])});
            skLineSegment(sketch, "E133.bottom", {"start": v(-2127.71, 5565.2) * mm, "end": v(-1257.71, 5565.2) * mm});
            skLineSegment(sketch, "E133.top", {"start": v(-2127.71, 5205.2) * mm, "end": v(-1257.71, 5205.2) * mm});
            skLineSegment(sketch, "E133.left", {"start": v(-2127.71, 5565.2) * mm, "end": v(-2127.71, 5205.2) * mm});
            skLineSegment(sketch, "E133.right", {"start": v(-1257.71, 5565.2) * mm, "end": v(-1257.71, 5205.2) * mm});
            skSolve(sketch);
        }
        {
            var Q0;
            Q0 = qSketchRegion(id + "F57", true);
            extrude(context, id + "F58", {"entities" : qUnion([Q0]), "depth" : 1225 * mm});
        }
        {
            var Q0;
            Q0=qCreatedBy(makeId("Top.planeOp"),FACE);
            var sketch = newSketch(context, id + "F59", { "sketchPlane" : qUnion([Q0])});
            skLineSegment(sketch, "E134.bottom", {"start": v(-2039.63, 8299.52) * mm, "end": v(-1169.63, 8299.52) * mm});
            skLineSegment(sketch, "E134.top", {"start": v(-2039.63, 8029.52) * mm, "end": v(-1169.63, 8029.52) * mm});
            skLineSegment(sketch, "E134.left", {"start": v(-2039.63, 8299.52) * mm, "end": v(-2039.63, 8029.52) * mm});
            skLineSegment(sketch, "E134.right", {"start": v(-1169.63, 8299.52) * mm, "end": v(-1169.63, 8029.52) * mm});
            skSolve(sketch);
        }
        {
            var Q0;
            Q0 = qSketchRegion(id + "F59", true);
            extrude(context, id + "F60", {"entities" : qUnion([Q0]), "depth" : 840 * mm});
        }
        {
            var Q0;
            Q0=qCreatedBy(makeId("Top.planeOp"),FACE);
            var sketch = newSketch(context, id + "F61", { "sketchPlane" : qUnion([Q0])});
            skLineSegment(sketch, "E135.bottom", {"start": v(-2193.88, 9652.08) * mm, "end": v(-1543.88, 9652.08) * mm});
            skLineSegment(sketch, "E135.top", {"start": v(-2193.88, 9102.08) * mm, "end": v(-1543.88, 9102.08) * mm});
            skLineSegment(sketch, "E135.left", {"start": v(-2193.88, 9652.08) * mm, "end": v(-2193.88, 9102.08) * mm});
            skLineSegment(sketch, "E135.right", {"start": v(-1543.88, 9652.08) * mm, "end": v(-1543.88, 9102.08) * mm});
            skLineSegment(sketch, "E136", {"start": v(-1643.88, 9652.08) * mm, "end": v(-1643.88, 9102.08) * mm});
            skLineSegment(sketch, "E137", {"start": v(-2193.88, 9652.08) * mm, "end": v(-2193.88, 9702.08) * mm});
            skLineSegment(sketch, "E138", {"start": v(-2193.88, 9702.08) * mm, "end": v(-1643.88, 9702.08) * mm});
            skLineSegment(sketch, "E139", {"start": v(-2193.88, 9102.08) * mm, "end": v(-2193.88, 9052.08) * mm});
            skLineSegment(sketch, "E140", {"start": v(-2193.88, 9052.08) * mm, "end": v(-1643.88, 9052.08) * mm});
            skLineSegment(sketch, "E141", {"start": v(-1643.88, 9702.08) * mm, "end": v(-1614.48, 9652.08) * mm});
            skLineSegment(sketch, "E142", {"start": v(-1614.48, 9652.08) * mm, "end": v(-1614.48, 9102.08) * mm, "construction": true});
            skLineSegment(sketch, "E143", {"start": v(-1614.48, 9102.08) * mm, "end": v(-1643.88, 9052.08) * mm});
            skSolve(sketch);
        }
        {
            var Q0;
            {var subQ0=sQuery(id+"F61.wireOp",EDGE,"E135.left");Q0=makeQuery(id+"F61.imprint","IMPRINT",FACE,{"disambiguationData":[TD([[makeQuery(id+"F61.imprint","IMPRINT",EDGE,{"derivedFrom":subQ0}),1.0]])]});}
            extrude(context, id + "F62", {"entities" : qUnion([Q0]), "oppositeDirection" : true, "depth" : 425 * mm});
        }
        {
            var Q0;
            {var subQ0=sQuery(id+"F61.wireOp",EDGE,"E135.left");Q0=makeQuery(id+"F61.imprint","IMPRINT",FACE,{"disambiguationData":[TD([[makeQuery(id+"F61.imprint","IMPRINT",EDGE,{"derivedFrom":subQ0}),1.0]])]});}
            extrude(context, id + "F63", {"entities" : qUnion([Q0]), "operationType" : NewBodyOperationType.ADD, "depth" : 25 * mm});
        }
        {
            var Q0;
            {var subQ0=sQuery(id+"F61.wireOp",EDGE,"E135.right");Q0=makeQuery(id+"F61.imprint","IMPRINT",FACE,{"disambiguationData":[TD([[makeQuery(id+"F61.imprint","IMPRINT",EDGE,{"derivedFrom":subQ0}),-1.0]])]});}
            extrude(context, id + "F64", {"entities" : qUnion([Q0]), "operationType" : NewBodyOperationType.ADD, "depth" : 500 * mm});
        }
        {
            var Q0;
            {var subQ0=sQuery(id+"F61.wireOp",EDGE,"E139");Q0=makeQuery(id+"F61.imprint","IMPRINT",FACE,{"disambiguationData":[TD([[makeQuery(id+"F61.imprint","IMPRINT",EDGE,{"derivedFrom":subQ0}),1.0]])]});}
            var Q1;
            {var subQ0=sQuery(id+"F61.wireOp",EDGE,"E137");Q1=makeQuery(id+"F61.imprint","IMPRINT",FACE,{"disambiguationData":[TD([[makeQuery(id+"F61.imprint","IMPRINT",EDGE,{"derivedFrom":subQ0}),-1.0]])]});}
            extrude(context, id + "F65", {"entities" : qUnion([Q0, Q1]), "operationType" : NewBodyOperationType.ADD, "depth" : 200 * mm});
        }
        {
            var Q0;
            {var subQ0=sQuery(id+"F61.wireOp",EDGE,"E139");var subQ1=sQuery(id+"F61.wireOp",EDGE,"E135.left");var subQ2=sQuery(id+"F61.wireOp",EDGE,"E135.top");Q0=makeQuery(id+"F63.boolean.opBoolean","MERGE",EDGE,{"derivedFrom":[makeQuery(id+"F62.opExtrude","SWEPT_EDGE",EDGE,{"disambiguationData":[OSD([subQ2,subQ1,subQ0])]}),makeQuery(id+"F63.opExtrude","SWEPT_EDGE",EDGE,{"disambiguationData":[OSD([subQ2,subQ1,subQ0])]})]});}
            var Q1;
            {var subQ0=sQuery(id+"F61.wireOp",EDGE,"E137");var subQ1=sQuery(id+"F61.wireOp",EDGE,"E135.left");var subQ2=sQuery(id+"F61.wireOp",EDGE,"E135.bottom");Q1=makeQuery(id+"F63.boolean.opBoolean","MERGE",EDGE,{"derivedFrom":[makeQuery(id+"F62.opExtrude","SWEPT_EDGE",EDGE,{"disambiguationData":[OSD([subQ2,subQ1,subQ0])]}),makeQuery(id+"F63.opExtrude","SWEPT_EDGE",EDGE,{"disambiguationData":[OSD([subQ2,subQ1,subQ0])]})]});}
            var Q2;
            {var subQ0=sQuery(id+"F61.wireOp",EDGE,"E136");var subQ1=sQuery(id+"F61.wireOp",EDGE,"E135.top");Q2=makeQuery(id+"F63.boolean.opBoolean","MERGE",EDGE,{"derivedFrom":[makeQuery(id+"F62.opExtrude","SWEPT_EDGE",EDGE,{"disambiguationData":[OSD([subQ1,subQ0])]}),makeQuery(id+"F63.opExtrude","SWEPT_EDGE",EDGE,{"disambiguationData":[OSD([subQ1,subQ0])]})]});}
            var Q3;
            {var subQ0=sQuery(id+"F61.wireOp",EDGE,"E136");var subQ1=sQuery(id+"F61.wireOp",EDGE,"E135.bottom");Q3=makeQuery(id+"F63.boolean.opBoolean","MERGE",EDGE,{"derivedFrom":[makeQuery(id+"F62.opExtrude","SWEPT_EDGE",EDGE,{"disambiguationData":[OSD([subQ1,subQ0])]}),makeQuery(id+"F63.opExtrude","SWEPT_EDGE",EDGE,{"disambiguationData":[OSD([subQ1,subQ0])]})]});}
            fillet(context, id + "F66", {"entities" : qUnion([Q0, Q1, Q2, Q3]), "radius" : 270 * mm, "tangentPropagation" : true, "allowEdgeOverflow" : false});
        }
        {
            var Q0;
            Q0=makeQuery(id+"F41.imprint","IMPRINT",FACE,{"disambiguationData":[TD([[makeQuery(id+"F41.imprint","IMPRINT",EDGE,{"derivedFrom":sQuery(id+"F41.wireOp",EDGE,"E117.bottom")}),-1.0]])]});
            extrude(context, id + "F67", {"entities" : qUnion([Q0]), "depth" : 720 * mm});
        }
        {
            var Q0;
            {var subQ0=sQuery(id+"F41.wireOp",EDGE,"E120");Q0=makeQuery(id+"F41.imprint","IMPRINT",FACE,{"disambiguationData":[TD([[makeQuery(id+"F41.imprint","IMPRINT",EDGE,{"derivedFrom":subQ0}),-1.0]])]});}
            extrude(context, id + "F68", {"entities" : qUnion([Q0]), "operationType" : NewBodyOperationType.ADD, "depth" : 650 * mm});
        }
    });
